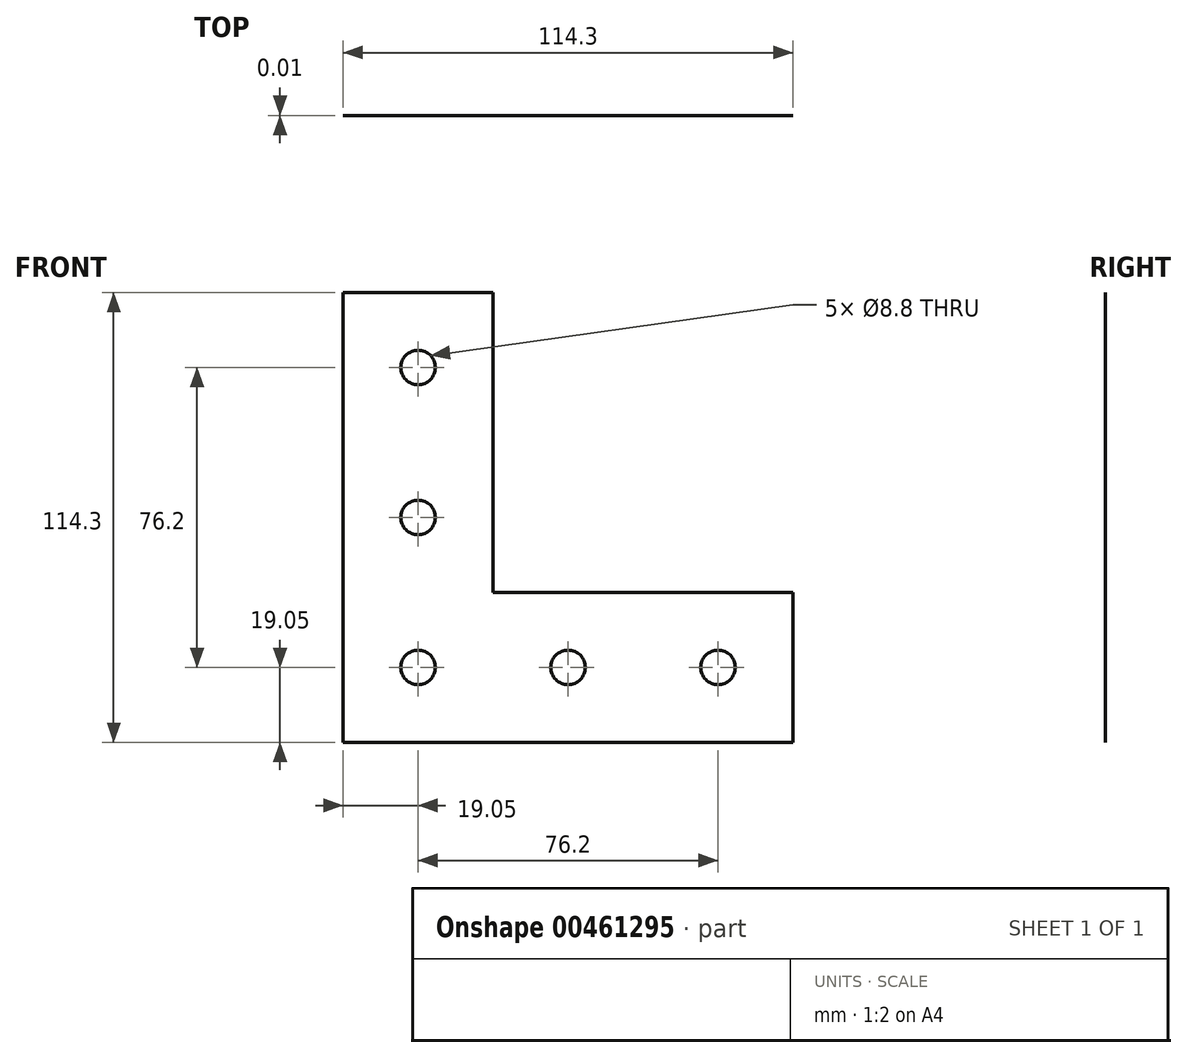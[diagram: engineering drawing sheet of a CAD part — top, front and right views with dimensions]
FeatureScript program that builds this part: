
annotation { "Feature Type Name" : "Feature", "Feature Type Description" : "" }
export const myFeature = defineFeature(function(context is Context, id is Id, definition is map)
    precondition{}
    {
        {
            var Q0;
            Q0=qCreatedBy(makeId("Front.planeOp"),FACE);
            var sketch = newSketch(context, id + "F0", { "sketchPlane" : qUnion([Q0])});
            skLineSegment(sketch, "E0", {"start": v(0, 0) * mm, "end": v(0, 114.3) * mm});
            skLineSegment(sketch, "E1", {"start": v(0, 114.3) * mm, "end": v(38.1, 114.3) * mm});
            skLineSegment(sketch, "E2", {"start": v(38.1, 114.3) * mm, "end": v(38.1, 38.1) * mm});
            skLineSegment(sketch, "E3", {"start": v(38.1, 38.1) * mm, "end": v(114.3, 38.1) * mm});
            skLineSegment(sketch, "E4", {"start": v(114.3, 38.1) * mm, "end": v(114.3, 0) * mm});
            skLineSegment(sketch, "E5", {"start": v(114.3, 0) * mm, "end": v(0, 0) * mm});
            skPoint(sketch, "E6", {"position": v(19.05, 95.25) * mm});
            skPoint(sketch, "E7", {"position": v(19.05, 57.15) * mm});
            skPoint(sketch, "E8", {"position": v(19.05, 19.05) * mm});
            skPoint(sketch, "E9", {"position": v(57.15, 19.05) * mm});
            skPoint(sketch, "E10", {"position": v(95.25, 19.05) * mm});
            skSolve(sketch);
        }
        {
            var Q0;
            Q0 = qSketchRegion(id + "F0", true);
            extrude(context, id + "F1", {"entities" : qUnion([Q0]), "oppositeDirection" : true, "depth" : 1 / 101.6 * mm, "offsetDistance" : 25 * mm});
        }
        {
            var Q0;
            Q0=sQuery(id+"F0.wireOp",VERTEX,"E6");
            var Q1;
            Q1=sQuery(id+"F0.wireOp",VERTEX,"E7");
            var Q2;
            Q2=sQuery(id+"F0.wireOp",VERTEX,"E8");
            var Q3;
            Q3=sQuery(id+"F0.wireOp",VERTEX,"E9");
            var Q4;
            Q4=sQuery(id+"F0.wireOp",VERTEX,"E10");
            var Q5;
            Q5=makeQuery(id+"F1.opExtrude","SWEPT_BODY",BODY,{"disambiguationData":[OSD([sQuery(id+"F0.wireOp",EDGE,"E0"),sQuery(id+"F0.wireOp",EDGE,"E1"),sQuery(id+"F0.wireOp",EDGE,"E2"),sQuery(id+"F0.wireOp",EDGE,"E3"),sQuery(id+"F0.wireOp",EDGE,"E4"),sQuery(id+"F0.wireOp",EDGE,"E5")])]});
            hole(context, id + "F2", {"style" : HoleStyle.SIMPLE, "endStyle" : HoleEndStyle.THROUGH, "standardTappedOrClearance" : lookupTablePath({ "standard" : "ISO", "fit" : "Normal", "size" : "M8", "type" : "Clearance" }), "standardBlindInLast" : lookupTablePath({ "fit" : "Standard", "standard" : "ISO", "size" : "M8", "type" : "Clearance" }), "holeDiameter" : 8.8 * mm, "majorDiameter" : 16 * mm, "isTappedThrough" : true, "tappedDepth" : 12 * mm, "tapClearance" : 3, "locations" : qUnion([Q0, Q1, Q2, Q3, Q4]), "scope" : qUnion([Q5])});
        }
    });
